# Revit family: Haworth_Superlight
name_source: partatom
category: Lighting Fixtures
revit_build: Autodesk Revit 2018 (Build: 20170223_1515(x64)
units: mm (PartAtom-declared; Revit-internal decimal feet)

## family parameters
Always vertical = Yes
Cut with Voids When Loaded = No
Light Source = Yes
OmniClass Number = 23.80.70.11.14
OmniClass Title = General Luminaries, Directional
Part Type = Normal
Room Calculation Point = No
Round Connector Dimension = Use Diameter
Shared = No
Work Plane-Based = No

## types (2) — shared parameters
Assembly Code = D5020200
Color Filter = 16777215
Connector Finish = Haworth _ Paint _ Collection Black
Dimming Lamp Color Temperature Shift = Incandescent Lamp Curve
Emit Shape Visible in Rendering = No
Emit from Circle Diameter = 24"
Glass Finish = Haworth _ Glass _ Clear
Light Source Symbol Size = 5"
Manufacturer = Haworth
Revision Number = 1
Size = Verify Final Dim. w/Haworth
URL = https://www.haworth.com
URL - Product = https://www.haworth.com
Warranty = https://www.haworth.com

## per-type parameters (varying)
| type | Actual Height | Description | Desk Lamp | Floor Lamp |
| HCPL-SLT1-17 | 25 3/4" | Haworth SuperLight Table Light | Yes | No |
| HCPL-SLF1-47 | 57 1/2" | Haworth SuperLight Floor Light | No | Yes |

note: column(s) folded — value = type name in every type: Model

## geometry (parser evidence)
native form markers: Sweep x3
no freeform markers — native parametric forms only
